# Revit family: SURVIVOR160xxWSxxxESGS0650x
name_source: partatom
category: Oprawy oświetleniowe
units: mm (PartAtom-declared; Revit-internal decimal feet)

## family parameters
Numer OmniClass = 23.80.70.11
Obiekt nadrzędny = Powierzchnia
Punkt obliczania pomieszczeń = Nie
Tnij formami wycięć po wczytaniu = Nie
Typ części = Normalny
Tytuł OmniClass = Luminaries for Internal Lighting
Współdzielony = Nie
Wymiar okrągłego złącza = Użyj średnicy
Źródło światła = Tak

## types (4) — shared parameters
Emituj kształt widoczny w renderingu = Nie
Emituj z długości prostokąta = 181 mm  [stored 0.593832 ft]
Emituj z szerokości prostokąta = 1528 mm  [stored 5.01312 ft]
Filtr koloru = 16777215
Kod zespołu = D5020200
Lampa = LED
Odchylenie kierunku = 90.00°
Plik sieci fotometrycznej = SURVIVOR_ESGS.IES
Producent = RIDI Leuchten GmbH
URL = www.ridi.de
Zmiana temperatury barwowej przyciemniania lampy = <Brak>
brand = RIDI
conformity mark = CE
electrical safety class = 1
height = 73 mm  [stored 0.239501 ft]
ingress protection (IP) code = IP65
length = 1600 mm  [stored 5.24934 ft]
nominal frequency = 50-60Hz
nominal voltage = 230
voltage type (AC, DC, UC) = AC
weight = 13,2
width = 240 mm  [stored 0.787402 ft]
zero-valued in all types: Domyślna rzędna

## per-type parameters (varying)
| type | Model | Obciążenie pozorne | rated input power |
| SURVIVOR160DAWS830ESGS0650 | 0632243 | 43 VA | 43 |
| SURVIVOR160NDWS830ESGS0650-RF | 0622243//420 | 42 VA | 42 |
| SURVIVOR160DAWS840ESGS0700 | 0632247 | 43 VA | 43 |
| SURVIVOR160NDWS840ESGS0700-RF | 0622247//420 | 42 VA | 42 |

note: column(s) folded — value = type name in every type: product name

note: [stored X ft] marks values corroborated as IEEE doubles in the binary element streams (Revit-internal decimal feet)
